# Revit family: Plumbing-Soap-Dispensers-Sloan-Valve-ESD-420_
name_source: partatom
category: Specialty Equipment
units: mm (PartAtom-declared; Revit-internal decimal feet)

## family parameters
Cut with Voids When Loaded = No
Host = Face
Maintain Annotation Orientation = No
OmniClass Number = 23.40.20.21.34
OmniClass Title = Soap Holders, Dispensers
Part Type = Normal
Room Calculation Point = No
Round Connector Dimension = Use Diameter
Shared = No

## types (1)
- Not a Type - Load Type Catalog!
    Apparent Load = 216 VA
    Assembly Code = D2010
    CW Connection = Yes
    Connector Description = Electrical Connection
    Current = 2 A
    Date Updated = 09.12.2024
    Default Elevation = 0 "
    Depth = 5.95 "
    Description = Sloan® Deck-Mounted Foam Soap Dispenser, Brushed Nickel Finish
    Edition number = 1
    HW Connection = Yes
    Height = 4.84 "
    Keynote = 15410
    Manufacturer = Sloan Valve
    Model = Model not specified - Load type catalog!
    Number of Poles = 1
    Part Number = 3346169
    Power Factor = 1
    Product Material = Sloan Valve - Finish - Brushed Nickel
    Product data url = https://bimobject.com
    URL = www.sloanvalve.com
    Vent Connection = No
    Version = 2
    Voltage = 120 V
    Waste Connection = No
    Width = 2.84 "

## geometry (parser evidence)
native form markers: Sweep x8
no freeform markers — native parametric forms only
